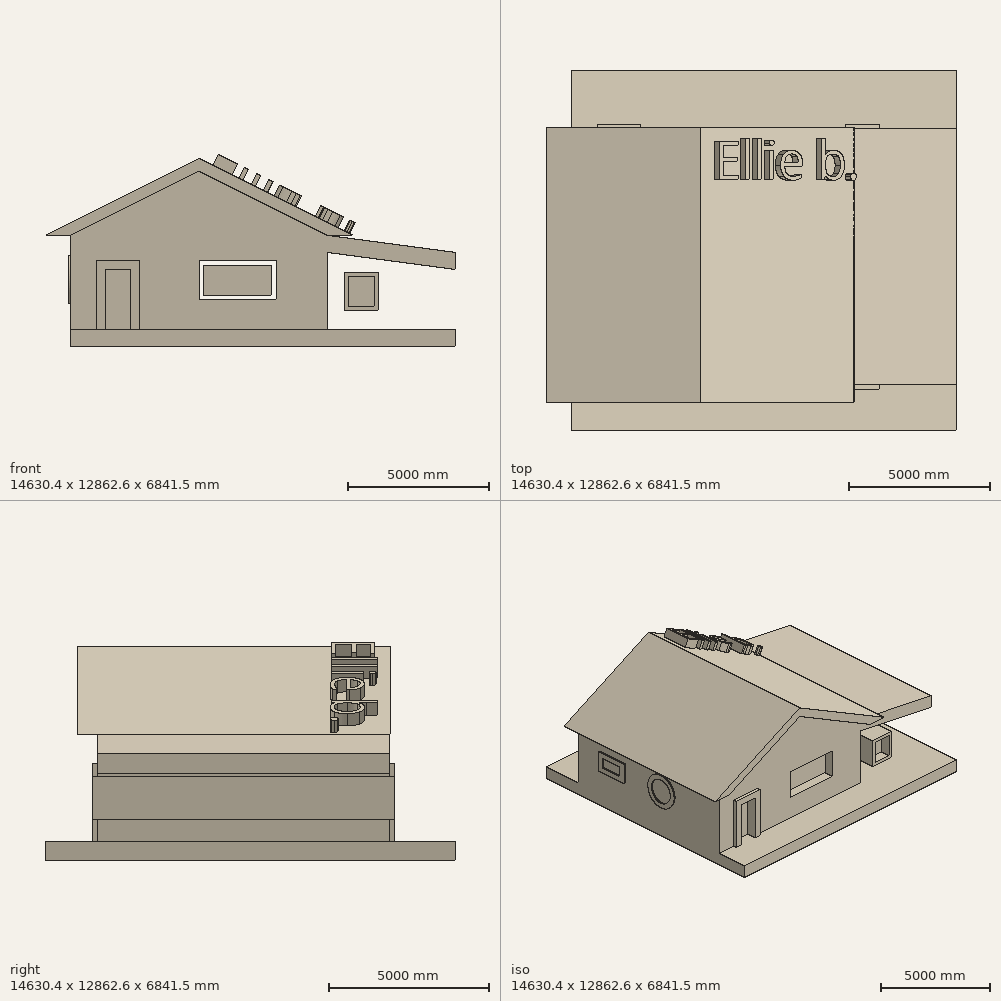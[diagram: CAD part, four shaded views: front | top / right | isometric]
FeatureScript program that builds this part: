
annotation { "Feature Type Name" : "Feature", "Feature Type Description" : "" }
export const myFeature = defineFeature(function(context is Context, id is Id, definition is map)
    precondition{}
    {
        {
            var Q0;
            Q0=qCreatedBy(makeId("Front.planeOp"),FACE);
            var sketch = newSketch(context, id + "F0", { "sketchPlane" : qUnion([Q0])});
            skLineSegment(sketch, "E0", {"start": v(0, 0) * mm, "end": v(-4572, 0) * mm});
            skLineSegment(sketch, "E1", {"start": v(0, 0) * mm, "end": v(4572, 0) * mm});
            skLineSegment(sketch, "E2", {"start": v(-4572, 0) * mm, "end": v(-4572, -3352.8) * mm});
            skLineSegment(sketch, "E3", {"start": v(-4572, -3352.8) * mm, "end": v(4572, -3352.8) * mm});
            skLineSegment(sketch, "E4", {"start": v(4572, -3352.8) * mm, "end": v(4572, 0) * mm});
            skLineSegment(sketch, "E5", {"start": v(0, 0) * mm, "end": v(0, 2286) * mm});
            skLineSegment(sketch, "E6", {"start": v(0, 2286) * mm, "end": v(-4572, 0) * mm});
            skLineSegment(sketch, "E7", {"start": v(0, 2286) * mm, "end": v(4572, 0) * mm});
            skLineSegment(sketch, "E8", {"start": v(-4572, 0) * mm, "end": v(-5486.4, 0) * mm});
            skLineSegment(sketch, "E9", {"start": v(4572, 0) * mm, "end": v(5486.4, 0) * mm});
            skLineSegment(sketch, "E10", {"start": v(0, 2286) * mm, "end": v(0, 2743.2) * mm});
            skLineSegment(sketch, "E11", {"start": v(-5486.4, 0) * mm, "end": v(0, 2743.2) * mm});
            skLineSegment(sketch, "E12", {"start": v(0, 2743.2) * mm, "end": v(5486.4, 0) * mm});
            skLineSegment(sketch, "E13", {"start": v(-4572, -3352.8) * mm, "end": v(-4572, -3962.4) * mm});
            skLineSegment(sketch, "E14", {"start": v(4572, -3352.8) * mm, "end": v(4572, -3962.4) * mm});
            skLineSegment(sketch, "E15", {"start": v(-4572, -3962.4) * mm, "end": v(4572, -3962.4) * mm});
            skLineSegment(sketch, "E16", {"start": v(4572, -3352.8) * mm, "end": v(9144, -3352.8) * mm});
            skLineSegment(sketch, "E17", {"start": v(4572, -3962.4) * mm, "end": v(9144, -3962.4) * mm});
            skLineSegment(sketch, "E18", {"start": v(9144, -3962.4) * mm, "end": v(9144, -3352.8) * mm});
            skLineSegment(sketch, "E19", {"start": v(9144, -3352.8) * mm, "end": v(9144, -609.6) * mm});
            skLineSegment(sketch, "E20", {"start": v(9144, -609.6) * mm, "end": v(4572, 0) * mm});
            skLineSegment(sketch, "E21", {"start": v(9144, -609.6) * mm, "end": v(9144, -1219.2) * mm});
            skLineSegment(sketch, "E22", {"start": v(4572, 0) * mm, "end": v(4572, -609.6) * mm});
            skLineSegment(sketch, "E23", {"start": v(4572, -609.6) * mm, "end": v(9144, -1219.2) * mm});
            skLineSegment(sketch, "E24", {"start": v(-3352.8, -3352.8) * mm, "end": v(-3352.8, -1219.2) * mm});
            skLineSegment(sketch, "E25", {"start": v(-3352.8, -1219.2) * mm, "end": v(-2438.4, -1219.2) * mm});
            skLineSegment(sketch, "E26", {"start": v(-2438.4, -1219.2) * mm, "end": v(-2438.4, -3352.8) * mm});
            skLineSegment(sketch, "E27.0", {"start": v(-2133.6, -914.4) * mm, "end": v(-2133.6, -3352.8) * mm});
            skLineSegment(sketch, "E27.1", {"start": v(-3657.6, -914.4) * mm, "end": v(-2133.6, -914.4) * mm});
            skLineSegment(sketch, "E27.2", {"start": v(-3657.6, -3352.8) * mm, "end": v(-3657.6, -914.4) * mm});
            skLineSegment(sketch, "E28", {"start": v(0, -914.4) * mm, "end": v(2743.2, -914.4) * mm});
            skLineSegment(sketch, "E29", {"start": v(2743.2, -914.4) * mm, "end": v(0, -914.4) * mm});
            skLineSegment(sketch, "E30", {"start": v(0, -914.4) * mm, "end": v(0, -2286) * mm});
            skLineSegment(sketch, "E31", {"start": v(0, -2286) * mm, "end": v(2743.2, -2286) * mm});
            skLineSegment(sketch, "E32", {"start": v(2743.2, -2286) * mm, "end": v(2743.2, -914.4) * mm});
            skLineSegment(sketch, "E33.0", {"start": v(2743.2, -909.4) * mm, "end": v(0, -909.4) * mm});
            skLineSegment(sketch, "E34.0", {"start": v(152.4, -1066.8) * mm, "end": v(152.4, -2133.6) * mm});
            skLineSegment(sketch, "E35.0", {"start": v(2590.8, -1066.8) * mm, "end": v(152.4, -1066.8) * mm});
            skLineSegment(sketch, "E36.0", {"start": v(152.4, -2133.6) * mm, "end": v(2590.8, -2133.6) * mm});
            skLineSegment(sketch, "E37.0", {"start": v(2590.8, -2133.6) * mm, "end": v(2590.8, -1066.8) * mm});
            skLineSegment(sketch, "E38.bottom", {"start": v(5181.6, -1313.69) * mm, "end": v(6400.8, -1313.69) * mm});
            skLineSegment(sketch, "E38.top", {"start": v(5181.6, -2685.29) * mm, "end": v(6400.8, -2685.29) * mm});
            skLineSegment(sketch, "E38.left", {"start": v(5181.6, -1313.69) * mm, "end": v(5181.6, -2685.29) * mm});
            skLineSegment(sketch, "E38.right", {"start": v(6400.8, -1313.69) * mm, "end": v(6400.8, -2685.29) * mm});
            skLineSegment(sketch, "E39.0", {"start": v(5334, -1466.09) * mm, "end": v(6248.4, -1466.09) * mm});
            skLineSegment(sketch, "E39.1", {"start": v(5334, -1466.09) * mm, "end": v(5334, -2532.89) * mm});
            skLineSegment(sketch, "E39.2", {"start": v(5334, -2532.89) * mm, "end": v(6248.4, -2532.89) * mm});
            skLineSegment(sketch, "E39.3", {"start": v(6248.4, -1466.09) * mm, "end": v(6248.4, -2532.89) * mm});
            skText(sketch, "E40", { "text": "Ellie B.", "fontName": "OpenSans-Regular.ttf"});
            const initialGuessF0  = {"E40": [-5.56117, 3.22748, 1, 0, 2.1042]};
            skSetInitialGuess(sketch, initialGuessF0);
            skSolve(sketch);
        }
        {
            var Q0;
            Q0=makeQuery(id+"F0.imprint","IMPRINT",FACE,{"disambiguationData":[TD([[makeQuery(id+"F0.imprint","IMPRINT",EDGE,{"derivedFrom":sQuery(id+"F0.wireOp",EDGE,"E6")}),-1.0]])]});
            var Q1;
            Q1=makeQuery(id+"F0.imprint","IMPRINT",FACE,{"disambiguationData":[TD([[makeQuery(id+"F0.imprint","IMPRINT",EDGE,{"derivedFrom":sQuery(id+"F0.wireOp",EDGE,"E7")}),1.0]])]});
            var Q2;
            Q2=makeQuery(id+"F0.imprint","IMPRINT",FACE,{"disambiguationData":[TD([[makeQuery(id+"F0.imprint","IMPRINT",EDGE,{"derivedFrom":sQuery(id+"F0.wireOp",EDGE,"E20")}),1.0]])]});
            extrude(context, id + "F1", {"entities" : qUnion([Q0, Q1, Q2]), "depth" : 9144 * mm, "offsetDistance" : 30.48 * mm});
        }
        {
            var Q0;
            Q0=makeQuery(id+"F0.imprint","IMPRINT",FACE,{"disambiguationData":[TD([[makeQuery(id+"F0.imprint","IMPRINT",EDGE,{"derivedFrom":sQuery(id+"F0.wireOp",EDGE,"E0")}),-1.0]])]});
            var Q1;
            Q1=makeQuery(id+"F0.imprint","IMPRINT",FACE,{"disambiguationData":[TD([[makeQuery(id+"F0.imprint","IMPRINT",EDGE,{"derivedFrom":sQuery(id+"F0.wireOp",EDGE,"E1")}),1.0]])]});
            extrude(context, id + "F2", {"entities" : qUnion([Q0, Q1]), "operationType" : NewBodyOperationType.ADD, "depth" : 9144 * mm, "offsetDistance" : 30.48 * mm});
        }
        {
            var Q0;
            Q0=makeQuery(id+"F0.imprint","IMPRINT",FACE,{"disambiguationData":[TD([[makeQuery(id+"F0.imprint","IMPRINT",EDGE,{"derivedFrom":sQuery(id+"F0.wireOp",EDGE,"E14")}),1.0]])]});
            extrude(context, id + "F3", {"entities" : qUnion([Q0]), "depth" : 9144 * mm, "offsetDistance" : 30.48 * mm});
        }
        {
            var Q0;
            Q0=makeQuery(id+"F0.imprint","IMPRINT",FACE,{"disambiguationData":[TD([[makeQuery(id+"F0.imprint","IMPRINT",EDGE,{"derivedFrom":sQuery(id+"F0.wireOp",EDGE,"E0")}),1.0]])]});
            var Q1;
            Q1=makeQuery(id+"F0.imprint","IMPRINT",FACE,{"disambiguationData":[TD([[makeQuery(id+"F0.imprint","IMPRINT",EDGE,{"derivedFrom":sQuery(id+"F0.wireOp",EDGE,"E4")}),-1.0]])]});
            extrude(context, id + "F4", {"entities" : qUnion([Q0, Q1]), "depth" : 9144 * mm, "offsetDistance" : 30.48 * mm});
        }
        {
            var Q0;
            {var subQ0=sQuery(id+"F0.wireOp",EDGE,"E24");Q0=makeQuery(id+"F0.imprint","IMPRINT",FACE,{"disambiguationData":[TD([[makeQuery(id+"F0.imprint","IMPRINT",EDGE,{"derivedFrom":subQ0}),-1.0]])]});}
            var Q1;
            Q1=makeQuery(id+"F0.imprint","IMPRINT",FACE,{"disambiguationData":[TD([[makeQuery(id+"F0.imprint","IMPRINT",EDGE,{"derivedFrom":sQuery(id+"F0.wireOp",EDGE,"E34.0")}),1.0]])]});
            var Q2;
            Q2=makeQuery(id+"F0.imprint","IMPRINT",FACE,{"disambiguationData":[TD([[makeQuery(id+"F0.imprint","IMPRINT",EDGE,{"derivedFrom":sQuery(id+"F0.wireOp",EDGE,"E39.0")}),-1.0]])]});
            extrude(context, id + "F5", {"entities" : qUnion([Q0, Q1, Q2]), "operationType" : NewBodyOperationType.ADD, "depth" : 30.48 * mm, "offsetDistance" : 30.48 * mm});
        }
        {
            var Q0;
            Q0=makeQuery(id+"F0.imprint","IMPRINT",FACE,{"disambiguationData":[TD([[makeQuery(id+"F0.imprint","IMPRINT",EDGE,{"derivedFrom":sQuery(id+"F0.wireOp",EDGE,"E38.bottom")}),-1.0]])]});
            var Q1;
            {var subQ0=sQuery(id+"F0.wireOp",EDGE,"E24");Q1=makeQuery(id+"F0.imprint","IMPRINT",FACE,{"disambiguationData":[TD([[makeQuery(id+"F0.imprint","IMPRINT",EDGE,{"derivedFrom":subQ0}),1.0]])]});}
            var Q2;
            Q2=makeQuery(id+"F0.imprint","IMPRINT",FACE,{"disambiguationData":[TD([[makeQuery(id+"F0.imprint","IMPRINT",EDGE,{"derivedFrom":sQuery(id+"F0.wireOp",EDGE,"E29")}),1.0]])]});
            extrude(context, id + "F6", {"entities" : qUnion([Q0, Q1, Q2]), "operationType" : NewBodyOperationType.ADD, "depth" : 914.4 * mm, "offsetDistance" : 30.48 * mm});
        }
        {
            var Q0;
            {var subQ0=sQuery(id+"F0.wireOp",EDGE,"E24");Q0=makeQuery(id+"F0.imprint","IMPRINT",FACE,{"disambiguationData":[TD([[makeQuery(id+"F0.imprint","IMPRINT",EDGE,{"derivedFrom":subQ0}),-1.0]])]});}
            var Q1;
            Q1=makeQuery(id+"F0.imprint","IMPRINT",FACE,{"disambiguationData":[TD([[makeQuery(id+"F0.imprint","IMPRINT",EDGE,{"derivedFrom":sQuery(id+"F0.wireOp",EDGE,"E34.0")}),1.0]])]});
            var Q2;
            Q2=makeQuery(id+"F0.imprint","IMPRINT",FACE,{"disambiguationData":[TD([[makeQuery(id+"F0.imprint","IMPRINT",EDGE,{"derivedFrom":sQuery(id+"F0.wireOp",EDGE,"E39.0")}),-1.0]])]});
            extrude(context, id + "F7", {"entities" : qUnion([Q0, Q1, Q2]), "operationType" : NewBodyOperationType.ADD, "depth" : 8839.2 * mm, "offsetDistance" : 30.48 * mm, "hasSecondDirection" : true, "secondDirectionOppositeDirection" : false, "secondDirectionDepth" : 792.48 * mm});
        }
        {
            var Q0;
            {var subQ0=sQuery(id+"F0.wireOp",EDGE,"E24");Q0=makeQuery(id+"F0.imprint","IMPRINT",FACE,{"disambiguationData":[TD([[makeQuery(id+"F0.imprint","IMPRINT",EDGE,{"derivedFrom":subQ0}),1.0]])]});}
            var Q1;
            Q1=makeQuery(id+"F0.imprint","IMPRINT",FACE,{"disambiguationData":[TD([[makeQuery(id+"F0.imprint","IMPRINT",EDGE,{"derivedFrom":sQuery(id+"F0.wireOp",EDGE,"E29")}),1.0]])]});
            var Q2;
            Q2=makeQuery(id+"F0.imprint","IMPRINT",FACE,{"disambiguationData":[TD([[makeQuery(id+"F0.imprint","IMPRINT",EDGE,{"derivedFrom":sQuery(id+"F0.wireOp",EDGE,"E38.bottom")}),-1.0]])]});
            extrude(context, id + "F8", {"entities" : qUnion([Q0, Q1, Q2]), "operationType" : NewBodyOperationType.ADD, "depth" : 9326.88 * mm, "offsetDistance" : 30.48 * mm, "hasSecondDirection" : true, "secondDirectionOppositeDirection" : true, "secondDirectionDepth" : 152.4 * mm});
        }
        {
            var Q0;
            {var subQ3=sQuery(id+"F0.wireOp",EDGE,"E13");Q0=makeQuery(id+"F0.imprint","IMPRINT",FACE,{"disambiguationData":[TD([[makeQuery(id+"F0.imprint","IMPRINT",EDGE,{"derivedFrom":subQ3}),1.0]])]});}
            var Q1;
            Q1=makeQuery(id+"F0.imprint","IMPRINT",FACE,{"disambiguationData":[TD([[makeQuery(id+"F0.imprint","IMPRINT",EDGE,{"derivedFrom":sQuery(id+"F0.wireOp",EDGE,"E14")}),1.0]])]});
            extrude(context, id + "F9", {"entities" : qUnion([Q0, Q1]), "operationType" : NewBodyOperationType.ADD, "depth" : 10789.92 * mm, "offsetDistance" : 30.48 * mm, "hasSecondDirection" : true, "secondDirectionOppositeDirection" : true, "secondDirectionDepth" : 2072.64 * mm});
        }
        {
            var Q0;
            Q0=makeQuery(id+"F1.opExtrude","SWEPT_FACE",FACE,{"disambiguationData":[OSD([sQuery(id+"F0.wireOp",EDGE,"E12")])]});
            var sketch = newSketch(context, id + "F10", { "sketchPlane" : qUnion([Q0])});
            skText(sketch, "E41", { "text": "Ellie b.", "fontName": "OpenSans-Regular.ttf"});
            const initialGuessF10  = {"E41": [-0.86593, -1.8324, 1, 0, 1.38458]};
            skSetInitialGuess(sketch, initialGuessF10);
            skSolve(sketch);
        }
        {
            var Q0;
            Q0=makeQuery(id+"F4.opExtrude","SWEPT_FACE",FACE,{"disambiguationData":[OSD([sQuery(id+"F0.wireOp",EDGE,"E2")])]});
            var sketch = newSketch(context, id + "F11", { "sketchPlane" : qUnion([Q0])});
            skLineSegment(sketch, "E42.bottom", {"start": v(1363.3, -1098.57) * mm, "end": v(3029.39, -1098.57) * mm});
            skLineSegment(sketch, "E42.top", {"start": v(1363.3, -2146.32) * mm, "end": v(3029.39, -2146.32) * mm});
            skLineSegment(sketch, "E42.left", {"start": v(1363.3, -1098.57) * mm, "end": v(1363.3, -2146.32) * mm});
            skLineSegment(sketch, "E42.right", {"start": v(3029.39, -1098.57) * mm, "end": v(3029.39, -2146.32) * mm});
            skCircle(sketch, "E43", {"center": v(5416.88, -1579.5) * mm, "radius": 852.95 * mm});
            skCircle(sketch, "E44", {"center": v(5416.88, -1579.5) * mm, "radius": 609.2 * mm});
            skLineSegment(sketch, "E45.bottom", {"start": v(1603.76, -1373.4) * mm, "end": v(2754.57, -1373.4) * mm});
            skLineSegment(sketch, "E45.top", {"start": v(1603.76, -1871.5) * mm, "end": v(2754.57, -1871.5) * mm});
            skLineSegment(sketch, "E45.left", {"start": v(1603.76, -1373.4) * mm, "end": v(1603.76, -1871.5) * mm});
            skLineSegment(sketch, "E45.right", {"start": v(2754.57, -1373.4) * mm, "end": v(2754.57, -1871.5) * mm});
            skSolve(sketch);
        }
        {
            var Q0;
            Q0=makeQuery(id+"F11.imprint","IMPRINT",FACE,{"disambiguationData":[TD([[makeQuery(id+"F11.imprint","IMPRINT",EDGE,{"derivedFrom":sQuery(id+"F11.wireOp",EDGE,"E42.bottom")}),-1.0]])]});
            var Q1;
            Q1=makeQuery(id+"F11.imprint","IMPRINT",FACE,{"disambiguationData":[TD([[makeQuery(id+"F11.imprint","IMPRINT",EDGE,{"derivedFrom":sQuery(id+"F11.wireOp",EDGE,"E43")}),1.0]])]});
            extrude(context, id + "F12", {"entities" : qUnion([Q0, Q1]), "operationType" : NewBodyOperationType.ADD, "depth" : 91.44 * mm, "offsetDistance" : 30.48 * mm});
        }
        {
            var Q0;
            Q0 = qSketchRegion(id + "F10", true);
            extrude(context, id + "F13", {"entities" : qUnion([Q0]), "operationType" : NewBodyOperationType.ADD, "depth" : 426.72 * mm, "offsetDistance" : 30.48 * mm});
        }
        {
            var Q0;
            Q0=makeQuery(id+"F0.imprint","IMPRINT",FACE,{"disambiguationData":[TD([[makeQuery(id+"F0.imprint","IMPRINT",EDGE,{"derivedFrom":sQuery(id+"F0.wireOp",EDGE,"E7")}),1.0]])]});
            var Q1;
            Q1=makeQuery(id+"F0.imprint","IMPRINT",FACE,{"disambiguationData":[TD([[makeQuery(id+"F0.imprint","IMPRINT",EDGE,{"derivedFrom":sQuery(id+"F0.wireOp",EDGE,"E6")}),-1.0]])]});
            extrude(context, id + "F14", {"entities" : qUnion([Q0, Q1]), "operationType" : NewBodyOperationType.ADD, "depth" : 9448.8 * mm, "offsetDistance" : 30.48 * mm});
        }
        {
            var Q0;
            {var subQ0=sQuery(id+"F0.wireOp",EDGE,"E13");Q0=makeQuery(id+"FenbulLQzgEoQMB_2.boolean.opBoolean","SPLIT",FACE,{"disambiguationData":[TD([makeQuery(id+"FenbulLQzgEoQMB_2.opExtrude","SWEPT_FACE",FACE,{"disambiguationData":[OSD([sQuery(id+"FfUclEAaTBIvHFH_2.wireOp",EDGE,"49e74fb6-fafb-4e89-be29-83f9679b5990.0")])]})])],"derivedFrom":makeQuery(id+"F9.boolean.opBoolean","MERGE",FACE,{"derivedFrom":[makeQuery(id+"F6.boolean.opBoolean","MERGE",FACE,{"derivedFrom":[makeQuery(id+"F3.opExtrude","SWEPT_FACE",FACE,{"disambiguationData":[OSD([subQ0])]}),makeQuery(id+"F4.opExtrude","SWEPT_FACE",FACE,{"disambiguationData":[OSD([sQuery(id+"F0.wireOp",EDGE,"E2")])]})]}),makeQuery(id+"F9.opExtrude","SWEPT_FACE",FACE,{"disambiguationData":[OSD([subQ0])]})]})});}
            extrude(context, id + "F15", {"entities" : qUnion([Q0]), "operationType" : NewBodyOperationType.ADD, "depth" : 30.48 * mm, "offsetDistance" : 30.48 * mm});
        }
        {
            var Q0;
            Q0=makeQuery(id+"F0.imprint","IMPRINT",FACE,{"disambiguationData":[TD([[makeQuery(id+"F0.imprint","IMPRINT",EDGE,{"derivedFrom":sQuery(id+"F0.wireOp",EDGE,"E6")}),-1.0]])]});
            var Q1;
            Q1=makeQuery(id+"F0.imprint","IMPRINT",FACE,{"disambiguationData":[TD([[makeQuery(id+"F0.imprint","IMPRINT",EDGE,{"derivedFrom":sQuery(id+"F0.wireOp",EDGE,"E7")}),1.0]])]});
            extrude(context, id + "F16", {"entities" : qUnion([Q0, Q1]), "operationType" : NewBodyOperationType.ADD, "depth" : 30.48 * mm, "offsetDistance" : 30.48 * mm});
        }
        {
            var Q0;
            Q0=makeQuery(id+"F0.imprint","IMPRINT",FACE,{"disambiguationData":[TD([[makeQuery(id+"F0.imprint","IMPRINT",EDGE,{"derivedFrom":sQuery(id+"F0.wireOp",EDGE,"E6")}),-1.0]])]});
            var Q1;
            Q1=makeQuery(id+"F0.imprint","IMPRINT",FACE,{"disambiguationData":[TD([[makeQuery(id+"F0.imprint","IMPRINT",EDGE,{"derivedFrom":sQuery(id+"F0.wireOp",EDGE,"E7")}),1.0]])]});
            extrude(context, id + "F17", {"entities" : qUnion([Q0, Q1]), "operationType" : NewBodyOperationType.ADD, "depth" : 9784.08 * mm, "offsetDistance" : 30.48 * mm, "hasSecondDirection" : true, "secondDirectionOppositeDirection" : true, "secondDirectionDepth" : 30.48 * mm});
        }
    });
